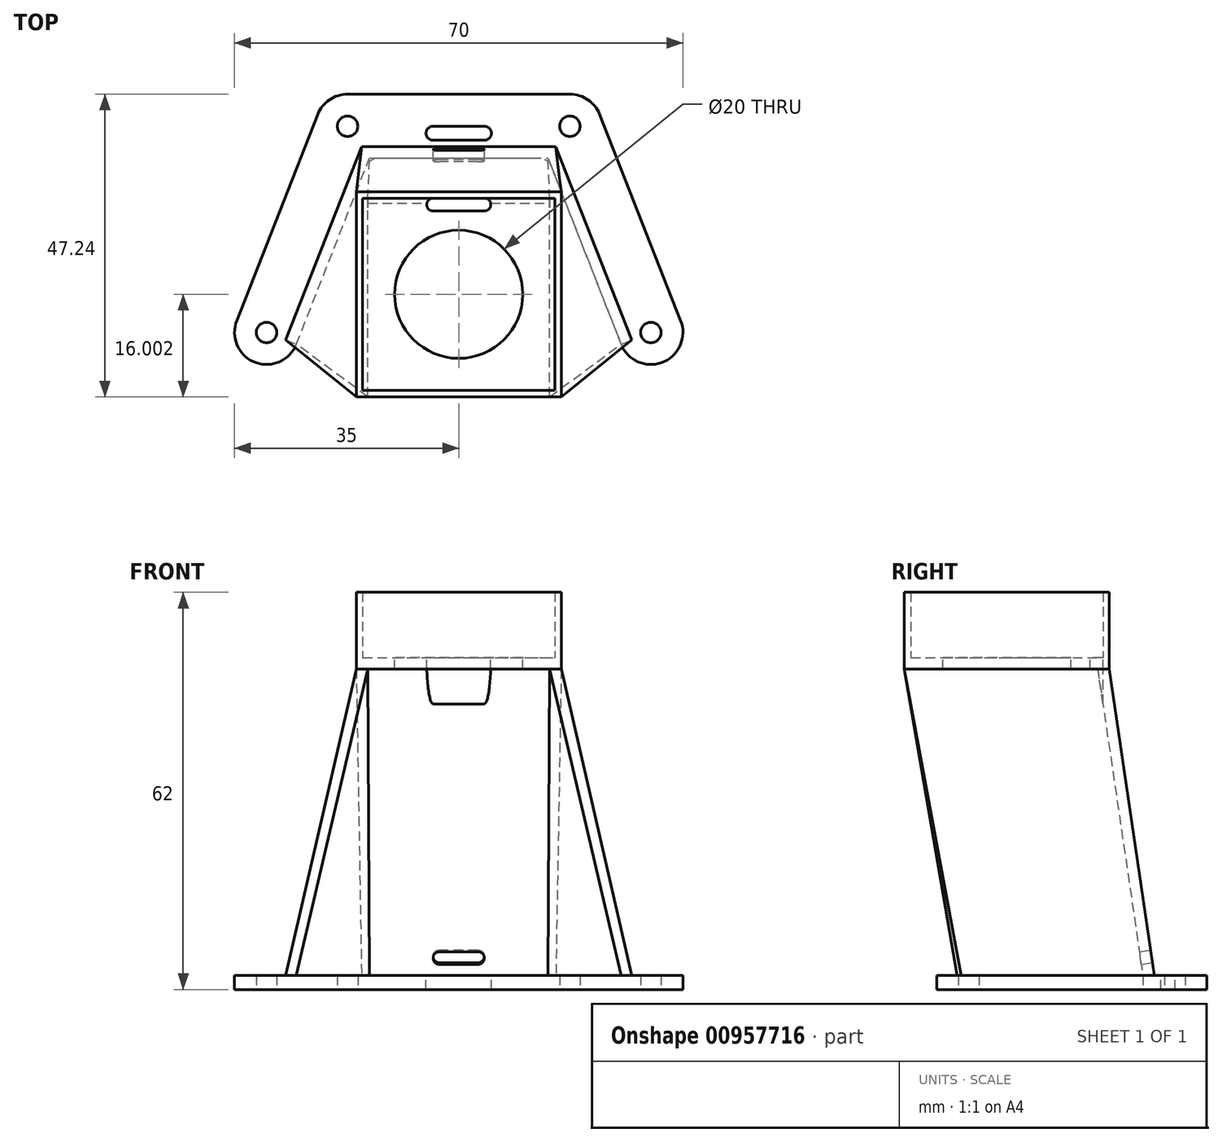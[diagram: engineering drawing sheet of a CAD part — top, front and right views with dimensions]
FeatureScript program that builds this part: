
annotation { "Feature Type Name" : "Feature", "Feature Type Description" : "" }
export const myFeature = defineFeature(function(context is Context, id is Id, definition is map)
    precondition{}
    {
        {
            var Q0;
            Q0=qCreatedBy(makeId("Top.planeOp"),FACE);
            var sketch = newSketch(context, id + "F0", { "sketchPlane" : qUnion([Q0])});
            skCircle(sketch, "E0", {"center": v(-17.35, 32.2) * mm, "radius": 1.6 * mm});
            skCircle(sketch, "E1", {"center": v(17.35, 32.2) * mm, "radius": 1.6 * mm});
            skCircle(sketch, "E2", {"center": v(30, 0) * mm, "radius": 1.6 * mm});
            skCircle(sketch, "E3", {"center": v(-30, 0) * mm, "radius": 1.6 * mm});
            skArc(sketch, "E4", {"start": v(-17.35, 37.2) * mm, "mid": v(-20.17, 36.33) * mm, "end": v(-22, 34.03) * mm});
            skArc(sketch, "E5", {"start": v(-34.65, 1.83) * mm, "mid": v(-31.83, -4.65) * mm, "end": v(-25.35, -1.83) * mm});
            skArc(sketch, "E6", {"start": v(22, 34.03) * mm, "mid": v(20.17, 36.33) * mm, "end": v(17.35, 37.2) * mm});
            skArc(sketch, "E7", {"start": v(25.35, -1.83) * mm, "mid": v(31.83, -4.65) * mm, "end": v(34.65, 1.83) * mm});
            skLineSegment(sketch, "E8", {"start": v(-34.65, 1.83) * mm, "end": v(-22, 34.03) * mm});
            skLineSegment(sketch, "E9", {"start": v(-17.35, 37.2) * mm, "end": v(17.35, 37.2) * mm});
            skLineSegment(sketch, "E10", {"start": v(22, 34.03) * mm, "end": v(34.65, 1.83) * mm});
            skLineSegment(sketch, "E11", {"start": v(-25.35, -1.83) * mm, "end": v(-13.94, 27.2) * mm});
            skLineSegment(sketch, "E12", {"start": v(-13.94, 27.2) * mm, "end": v(13.94, 27.2) * mm});
            skLineSegment(sketch, "E13", {"start": v(13.94, 27.2) * mm, "end": v(25.35, -1.83) * mm});
            skPoint(sketch, "E14", {"position": v(-13.94, 27.2) * mm});
            skPoint(sketch, "E15", {"position": v(13.94, 27.2) * mm});
            skSolve(sketch);
        }
        {
            var Q0;
            Q0 = qSketchRegion(id + "F0", true);
            extrude(context, id + "F1", {"entities" : qUnion([Q0]), "depth" : 2.2 * mm, "offsetDistance" : 25 * mm});
        }
        {
            var Q0;
            Q0=qCreatedBy(makeId("Top.planeOp"),FACE);
            cPlane(context, id + "F2", {"entities" : qUnion([Q0]), "cplaneType" : CPlaneType.OFFSET, "offset" : 50 * mm, "width" : 150 * mm, "height" : 150 * mm});
        }
        {
            var Q0;
            Q0=qCreatedBy(id+"F2.planeOp",FACE);
            var sketch = newSketch(context, id + "F3", { "sketchPlane" : qUnion([Q0])});
            skLineSegment(sketch, "E16.bottom", {"start": v(-16, -10.04) * mm, "end": v(16, -10.04) * mm});
            skLineSegment(sketch, "E16.top", {"start": v(-16, 21.96) * mm, "end": v(16, 21.96) * mm});
            skLineSegment(sketch, "E16.left", {"start": v(-16, -10.04) * mm, "end": v(-16, 21.96) * mm});
            skLineSegment(sketch, "E16.right", {"start": v(16, -10.04) * mm, "end": v(16, 21.96) * mm});
            skLineSegment(sketch, "E17.0", {"start": v(-25.35, -1.83) * mm, "end": v(-13.94, 27.2) * mm, "construction": true});
            skLineSegment(sketch, "E18.0", {"start": v(13.94, 27.2) * mm, "end": v(25.35, -1.83) * mm, "construction": true});
            skLineSegment(sketch, "E19.0", {"start": v(-15, 20.96) * mm, "end": v(15, 20.96) * mm});
            skLineSegment(sketch, "E19.1", {"start": v(-15, -9.04) * mm, "end": v(-15, 20.96) * mm});
            skLineSegment(sketch, "E19.2", {"start": v(-15, -9.04) * mm, "end": v(15, -9.04) * mm});
            skLineSegment(sketch, "E19.3", {"start": v(15, -9.04) * mm, "end": v(15, 20.96) * mm});
            skSolve(sketch);
        }
        {
            var Q0;
            Q0=makeQuery(id+"F1.opExtrude","CAP_FACE",FACE,{"disambiguationData":[OSD([sQuery(id+"F0.wireOp",EDGE,"E0"),sQuery(id+"F0.wireOp",EDGE,"E1"),sQuery(id+"F0.wireOp",EDGE,"E2"),sQuery(id+"F0.wireOp",EDGE,"E3"),sQuery(id+"F0.wireOp",EDGE,"E4"),sQuery(id+"F0.wireOp",EDGE,"E5"),sQuery(id+"F0.wireOp",EDGE,"E6"),sQuery(id+"F0.wireOp",EDGE,"E7"),sQuery(id+"F0.wireOp",EDGE,"E8"),sQuery(id+"F0.wireOp",EDGE,"E9"),sQuery(id+"F0.wireOp",EDGE,"E10"),sQuery(id+"F0.wireOp",EDGE,"E11"),sQuery(id+"F0.wireOp",EDGE,"E12"),sQuery(id+"F0.wireOp",EDGE,"E13")])],"isStart":false});
            var sketch = newSketch(context, id + "F4", { "sketchPlane" : qUnion([Q0])});
            skLineSegment(sketch, "E20.0", {"start": v(-25.35, -1.83) * mm, "end": v(-13.94, 27.2) * mm});
            skLineSegment(sketch, "E21.0", {"start": v(-13.94, 27.2) * mm, "end": v(13.94, 27.2) * mm});
            skLineSegment(sketch, "E22.0", {"start": v(13.94, 27.2) * mm, "end": v(25.35, -1.83) * mm});
            skLineSegment(sketch, "E23.0", {"start": v(15.17, 29) * mm, "end": v(27.02, -1.17) * mm});
            skLineSegment(sketch, "E23.1", {"start": v(-15.17, 29) * mm, "end": v(15.17, 29) * mm});
            skLineSegment(sketch, "E23.2", {"start": v(-27.02, -1.17) * mm, "end": v(-15.17, 29) * mm});
            skLineSegment(sketch, "E24", {"start": v(-27.02, -1.17) * mm, "end": v(-25.35, -1.83) * mm});
            skLineSegment(sketch, "E25", {"start": v(25.35, -1.83) * mm, "end": v(27.02, -1.17) * mm});
            skSolve(sketch);
        }
        {
            var Q0;
            Q0=makeQuery(id+"F3.imprint","IMPRINT",FACE,{"disambiguationData":[TD([[makeQuery(id+"F3.imprint","IMPRINT",EDGE,{"derivedFrom":sQuery(id+"F3.wireOp",EDGE,"E19.0")}),-1.0]])]});
            extrude(context, id + "F5", {"entities" : qUnion([Q0]), "depth" : 1.8 * mm, "offsetDistance" : 25 * mm});
        }
        {
            var Q0;
            Q0=makeQuery(id+"F3.imprint","IMPRINT",FACE,{"disambiguationData":[TD([[makeQuery(id+"F3.imprint","IMPRINT",EDGE,{"derivedFrom":sQuery(id+"F3.wireOp",EDGE,"E16.bottom")}),1.0]])]});
            extrude(context, id + "F6", {"entities" : qUnion([Q0]), "operationType" : NewBodyOperationType.ADD, "depth" : 12 * mm, "offsetDistance" : 25 * mm});
        }
        {
            var Q0;
            {var subQ0=sQuery(id+"F3.wireOp",EDGE,"E19.3");var subQ1=sQuery(id+"F3.wireOp",EDGE,"E19.2");var subQ2=sQuery(id+"F3.wireOp",EDGE,"E19.1");var subQ3=sQuery(id+"F3.wireOp",EDGE,"E19.0");Q0=makeQuery(id+"F6.boolean.opBoolean","MERGE",FACE,{"derivedFrom":[makeQuery(id+"F5.opExtrude","CAP_FACE",FACE,{"disambiguationData":[OSD([subQ3,subQ2,subQ1,subQ0])],"isStart":true}),makeQuery(id+"F6.opExtrude","CAP_FACE",FACE,{"disambiguationData":[OSD([sQuery(id+"F3.wireOp",EDGE,"E16.bottom"),sQuery(id+"F3.wireOp",EDGE,"E16.top"),sQuery(id+"F3.wireOp",EDGE,"E16.left"),sQuery(id+"F3.wireOp",EDGE,"E16.right"),subQ3,subQ2,subQ1,subQ0])],"isStart":true})]});}
            var sketch = newSketch(context, id + "F7", { "sketchPlane" : qUnion([Q0])});
            skLineSegment(sketch, "E26.0", {"start": v(-16, 10.04) * mm, "end": v(-16, -21.96) * mm});
            skLineSegment(sketch, "E27.0", {"start": v(-16, -21.96) * mm, "end": v(16, -21.96) * mm});
            skLineSegment(sketch, "E28.0", {"start": v(16, 10.04) * mm, "end": v(16, -21.96) * mm});
            skLineSegment(sketch, "E29.0", {"start": v(14.2, 10.04) * mm, "end": v(14.2, -20.16) * mm});
            skLineSegment(sketch, "E29.1", {"start": v(-14.2, -20.16) * mm, "end": v(14.2, -20.16) * mm});
            skLineSegment(sketch, "E29.2", {"start": v(-14.2, 10.04) * mm, "end": v(-14.2, -20.16) * mm});
            skLineSegment(sketch, "E30", {"start": v(-14.2, 10.04) * mm, "end": v(-16, 10.04) * mm});
            skLineSegment(sketch, "E31", {"start": v(16, 10.04) * mm, "end": v(14.2, 10.04) * mm});
            skSolve(sketch);
        }
        {
            var Q0;
            Q0=makeQuery(id+"F7.imprint","IMPRINT",FACE,{"disambiguationData":[TD([[makeQuery(id+"F7.imprint","IMPRINT",EDGE,{"derivedFrom":sQuery(id+"F7.wireOp",EDGE,"E26.0")}),1.0]])]});
            var Q1;
            Q1=makeQuery(id+"F4.imprint","IMPRINT",FACE,{"disambiguationData":[TD([[makeQuery(id+"F4.imprint","IMPRINT",EDGE,{"derivedFrom":sQuery(id+"F4.wireOp",EDGE,"E20.0")}),1.0]])]});
            loft(context, id + "F8", {"sheetProfilesArray" : [{ "sheetProfileEntities" : qUnion([Q0]) }, { "sheetProfileEntities" : qUnion([Q1]) }]});
        }
        {
            var Q0;
            Q0=makeQuery(id+"F5.opExtrude","CAP_FACE",FACE,{"disambiguationData":[OSD([sQuery(id+"F3.wireOp",EDGE,"E19.0"),sQuery(id+"F3.wireOp",EDGE,"E19.1"),sQuery(id+"F3.wireOp",EDGE,"E19.2"),sQuery(id+"F3.wireOp",EDGE,"E19.3")])],"isStart":false});
            var sketch = newSketch(context, id + "F9", { "sketchPlane" : qUnion([Q0])});
            skLineSegment(sketch, "E32.bottom", {"start": v(-4, 20.96) * mm, "end": v(4, 20.96) * mm});
            skLineSegment(sketch, "E32.top", {"start": v(-4, 18.96) * mm, "end": v(4, 18.96) * mm});
            skArc(sketch, "E33", {"start": v(-4, 18.96) * mm, "mid": v(-5, 19.96) * mm, "end": v(-4, 20.96) * mm});
            skArc(sketch, "E34", {"start": v(4, 18.96) * mm, "mid": v(5, 19.96) * mm, "end": v(4, 20.96) * mm});
            skSolve(sketch);
        }
        {
            var Q0;
            Q0 = qSketchRegion(id + "F9", true);
            extrude(context, id + "F10", {"entities" : qUnion([Q0]), "operationType" : NewBodyOperationType.REMOVE, "endBound" : BoundingType.THROUGH_ALL, "oppositeDirection" : true, "depth" : 25 * mm, "offsetDistance" : 25 * mm});
        }
        {
            var Q0;
            Q0=makeQuery(id+"F1.opExtrude","CAP_FACE",FACE,{"disambiguationData":[OSD([sQuery(id+"F0.wireOp",EDGE,"E0"),sQuery(id+"F0.wireOp",EDGE,"E1"),sQuery(id+"F0.wireOp",EDGE,"E2"),sQuery(id+"F0.wireOp",EDGE,"E3"),sQuery(id+"F0.wireOp",EDGE,"E4"),sQuery(id+"F0.wireOp",EDGE,"E5"),sQuery(id+"F0.wireOp",EDGE,"E6"),sQuery(id+"F0.wireOp",EDGE,"E7"),sQuery(id+"F0.wireOp",EDGE,"E8"),sQuery(id+"F0.wireOp",EDGE,"E9"),sQuery(id+"F0.wireOp",EDGE,"E10"),sQuery(id+"F0.wireOp",EDGE,"E11"),sQuery(id+"F0.wireOp",EDGE,"E12"),sQuery(id+"F0.wireOp",EDGE,"E13")])],"isStart":false});
            var sketch = newSketch(context, id + "F11", { "sketchPlane" : qUnion([Q0])});
            skLineSegment(sketch, "E35.bottom", {"start": v(4, 30) * mm, "end": v(-4, 30) * mm});
            skLineSegment(sketch, "E35.top", {"start": v(4, 32.2) * mm, "end": v(-4, 32.2) * mm});
            skArc(sketch, "E36", {"start": v(4, 30) * mm, "mid": v(5.1, 31.1) * mm, "end": v(4, 32.2) * mm});
            skArc(sketch, "E37", {"start": v(-4, 30) * mm, "mid": v(-5.1, 31.1) * mm, "end": v(-4, 32.2) * mm});
            skCircle(sketch, "E38.0", {"center": v(17.35, 32.2) * mm, "radius": 1.6 * mm, "construction": true});
            skCircle(sketch, "E39.0", {"center": v(-17.35, 32.2) * mm, "radius": 1.6 * mm, "construction": true});
            skLineSegment(sketch, "E40", {"start": v(17.35, 32.2) * mm, "end": v(-17.35, 32.2) * mm, "construction": true});
            skSolve(sketch);
        }
        {
            var Q0;
            Q0 = qSketchRegion(id + "F11", true);
            extrude(context, id + "F12", {"entities" : qUnion([Q0]), "operationType" : NewBodyOperationType.REMOVE, "endBound" : BoundingType.THROUGH_ALL, "oppositeDirection" : true, "depth" : 25 * mm, "offsetDistance" : 25 * mm});
        }
        {
            var Q0;
            Q0=makeQuery(id+"F8.opLoft","SWEPT_FACE",FACE,{"disambiguationData":[OSD([sQuery(id+"F4.wireOp",EDGE,"E23.0"),sQuery(id+"F4.wireOp",EDGE,"E23.1"),sQuery(id+"F4.wireOp",EDGE,"E23.2"),sQuery(id+"F7.wireOp",EDGE,"E26.0"),sQuery(id+"F7.wireOp",EDGE,"E27.0"),sQuery(id+"F7.wireOp",EDGE,"E28.0")])]});
            var sketch = newSketch(context, id + "F13", { "sketchPlane" : qUnion([Q0])});
            skLineSegment(sketch, "E41.bottom", {"start": v(-3, 1.95) * mm, "end": v(3, 1.95) * mm});
            skLineSegment(sketch, "E41.top", {"start": v(-3, -0.05) * mm, "end": v(3, -0.05) * mm});
            skArc(sketch, "E42", {"start": v(-3, 1.95) * mm, "mid": v(-4, 0.95) * mm, "end": v(-3, -0.05) * mm});
            skArc(sketch, "E43", {"start": v(3, 1.95) * mm, "mid": v(4, 0.95) * mm, "end": v(3, -0.05) * mm});
            skSolve(sketch);
        }
        {
            var Q0;
            Q0 = qSketchRegion(id + "F13", true);
            extrude(context, id + "F14", {"entities" : qUnion([Q0]), "operationType" : NewBodyOperationType.REMOVE, "endBound" : BoundingType.THROUGH_ALL, "oppositeDirection" : true, "depth" : 25 * mm, "offsetDistance" : 25 * mm});
        }
        {
            var Q0;
            Q0=makeQuery(id+"F5.opExtrude","CAP_FACE",FACE,{"disambiguationData":[OSD([sQuery(id+"F3.wireOp",EDGE,"E19.0"),sQuery(id+"F3.wireOp",EDGE,"E19.1"),sQuery(id+"F3.wireOp",EDGE,"E19.2"),sQuery(id+"F3.wireOp",EDGE,"E19.3")])],"isStart":false});
            var sketch = newSketch(context, id + "F15", { "sketchPlane" : qUnion([Q0])});
            skCircle(sketch, "E44", {"center": v(0, 5.96) * mm, "radius": 10 * mm});
            skLineSegment(sketch, "E45", {"start": v(15, 20.96) * mm, "end": v(-15, -9.04) * mm, "construction": true});
            skSolve(sketch);
        }
        {
            var Q0;
            Q0=makeQuery(id+"F15.imprint","IMPRINT",FACE,{"disambiguationData":[TD([[makeQuery(id+"F15.imprint","IMPRINT",EDGE,{"derivedFrom":sQuery(id+"F15.wireOp",EDGE,"E44")}),1.0]])]});
            extrude(context, id + "F16", {"entities" : qUnion([Q0]), "operationType" : NewBodyOperationType.REMOVE, "endBound" : BoundingType.THROUGH_ALL, "oppositeDirection" : true, "depth" : 25 * mm, "offsetDistance" : 25 * mm});
        }
        {
            var Q0;
            Q0=makeQuery(id+"F8.opLoft","MID_CAP_EDGE",EDGE,{"disambiguationData":[OSD([sQuery(id+"F3.wireOp",EDGE,"E16.bottom"),sQuery(id+"F7.wireOp",EDGE,"E29.0"),sQuery(id+"F7.wireOp",EDGE,"E29.1"),sQuery(id+"F7.wireOp",EDGE,"E31")])],"capPos":0.0});
            var Q1;
            Q1=makeQuery(id+"F8.opLoft","MID_CAP_EDGE",EDGE,{"disambiguationData":[OSD([sQuery(id+"F3.wireOp",EDGE,"E16.bottom"),sQuery(id+"F7.wireOp",EDGE,"E29.1"),sQuery(id+"F7.wireOp",EDGE,"E29.2"),sQuery(id+"F7.wireOp",EDGE,"E30")])],"capPos":0.0});
            var Q2;
            Q2=makeQuery(id+"F8.opLoft","SWEPT_EDGE",EDGE,{"disambiguationData":[OSD([sQuery(id+"F4.wireOp",EDGE,"E20.0"),sQuery(id+"F4.wireOp",EDGE,"E21.0"),sQuery(id+"F7.wireOp",EDGE,"E29.1"),sQuery(id+"F7.wireOp",EDGE,"E29.2")])]});
            var Q3;
            Q3=makeQuery(id+"F8.opLoft","SWEPT_EDGE",EDGE,{"disambiguationData":[OSD([sQuery(id+"F4.wireOp",EDGE,"E21.0"),sQuery(id+"F4.wireOp",EDGE,"E22.0"),sQuery(id+"F7.wireOp",EDGE,"E29.0"),sQuery(id+"F7.wireOp",EDGE,"E29.1")])]});
            var Q4;
            Q4=makeQuery(id+"F1.opExtrude","SWEPT_EDGE",EDGE,{"disambiguationData":[OSD([sQuery(id+"F0.wireOp",EDGE,"E12"),sQuery(id+"F0.wireOp",EDGE,"E13")])]});
            var Q5;
            Q5=makeQuery(id+"F1.opExtrude","SWEPT_EDGE",EDGE,{"disambiguationData":[OSD([sQuery(id+"F0.wireOp",EDGE,"E11"),sQuery(id+"F0.wireOp",EDGE,"E12")])]});
            fillet(context, id + "F17", {"entities" : qUnion([Q0, Q1, Q2, Q3, Q4, Q5]), "radius" : 2 * mm, "tangentPropagation" : true, "allowEdgeOverflow" : false});
        }
    });
